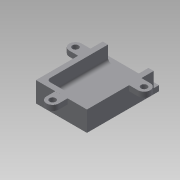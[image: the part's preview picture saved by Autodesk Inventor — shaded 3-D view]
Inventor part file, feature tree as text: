
AUTODESK INVENTOR PART (.ipt)
format: ipt  version: 2015 SP1 (Build 190203100, 203)  size: 252,928 bytes
history: native  units: mm
features: extrude x14, sketch x14, projected_geometry x10, fillet x1
ambient origin geometry x8: Origin, YZ Plane, XZ Plane, XY Plane, X Axis, Y Axis, Z Axis, Center Point
bodies: Solid1 (feature_tree)
feature tree (39):
  extrude  "Extrusion1"  Depth=1.0mm TaperAngle=0.0deg
  sketch  "Sketch2"  dims[d4=1.0mm d5=2.0mm d6=2.0mm]
  extrude  "Extrusion6"  Depth=2.0mm
  fillet  "Fillet1"  Radius=2.0mm
  extrude  "Extrusion8"  Depth=2.0mm
  extrude  "Extrusion9"  Depth=37.0mm
  extrude  "Extrusion10"  Depth=8.5mm TaperAngle=0.0deg
  extrude  "Extrusion11"  Depth=2.0mm TaperAngle=0.0deg
  extrude  "Extrusion12"  Depth=2.0mm TaperAngle=0.0deg
  sketch  "Sketch9"  dims[d63=2.0mm d64=0.0mm d65=4.0mm d66=0.0mm]
  extrude  "Extrusion15"  Depth=2.0mm TaperAngle=0.0deg
  extrude  "Extrusion16"  Depth=11.5mm TaperAngle=0.0deg
  extrude  "Extrusion17"  Depth=3.0mm TaperAngle=0.0deg
  extrude  "Extrusion18"  Depth=2.0mm TaperAngle=0.0deg
  extrude  "Extrusion19"  Depth=2.0mm TaperAngle=0.0deg
  extrude  "Extrusion20"  Depth=2.0mm TaperAngle=0.0deg
  extrude  "Extrusion21"  [1 undecoded]
  sketch  "Sketch1"  dims[d0=25.0mm d2=1.0mm d3=0.0mm]
  sketch  "Sketch4"  dims[d7=2.0mm d8=1.0mm]
  projected_geometry  "Projected Loop2"
  sketch  "Sketch5"  dims[d10=37.0mm d11=37.0mm]
  projected_geometry  "Projected Loop3"
  sketch  "Sketch6"  dims[d12=40.0mm d31=8.5mm d32=0.0mm]
  projected_geometry  "Projected Loop4"
  sketch  "Sketch7"  dims[d33=2.0mm d57=2.0mm d58=0.0mm]
  projected_geometry  "Projected Loop5"
  sketch  "Sketch8"  dims[d59=2.0mm d60=0.0mm d61=2.0mm d62=0.0mm]
  projected_geometry  "Projected Loop6"
  projected_geometry  "Projected Loop7"
  projected_geometry  "Projected Loop8"
  sketch  "Sketch14"  dims[d71=11.0mm d72=0.0mm d73=11.5mm d74=0.0mm]
  sketch  "Sketch16"  dims[d76=3.0mm d77=0.0mm d78=1.0mm d79=0.0mm]
  sketch  "Sketch17"  dims[d80=2.0mm d81=2.0mm d82=0.0mm]
  projected_geometry  "Projected Loop9"
  sketch  "Sketch18"  dims[d83=2.0mm d84=2.0mm d85=0.0mm]
  sketch  "Sketch19"  dims[d86=2.0mm d87=2.0mm d88=0.0mm]
  projected_geometry  "Projected Loop10"
  projected_geometry  "Projected Loop11"
  sketch  "Sketch20"
note: 1 required parameter value undecoded (feature->parameter linkage not recoverable at this tier; creation-order binding heuristic only, values carry confidence <= 0.55)
